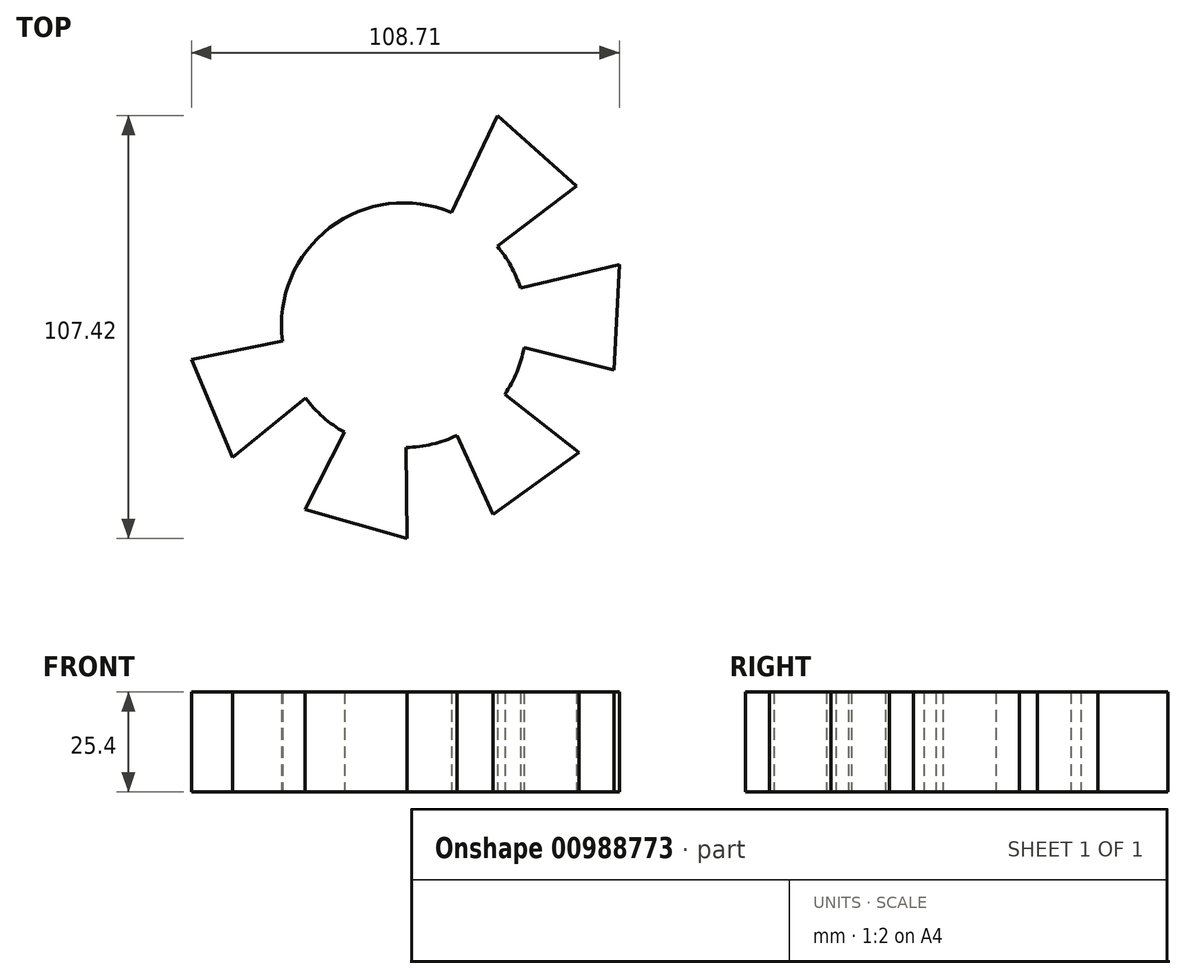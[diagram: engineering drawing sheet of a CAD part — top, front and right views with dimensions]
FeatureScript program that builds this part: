
annotation { "Feature Type Name" : "Feature", "Feature Type Description" : "" }
export const myFeature = defineFeature(function(context is Context, id is Id, definition is map)
    precondition{}
    {
        {
            var Q0;
            Q0=qCreatedBy(makeId("Top.planeOp"),FACE);
            var sketch = newSketch(context, id + "F0", { "sketchPlane" : qUnion([Q0])});
            skCircle(sketch, "E0", {"center": v(0, -2.16) * mm, "radius": 31.08 * mm});
            skLineSegment(sketch, "E1", {"start": v(12.13, 26.46) * mm, "end": v(23.74, 51.09) * mm});
            skLineSegment(sketch, "E2", {"start": v(23.74, 51.09) * mm, "end": v(43.9, 33.24) * mm});
            skLineSegment(sketch, "E3", {"start": v(43.9, 33.24) * mm, "end": v(23.74, 17.9) * mm});
            skLineSegment(sketch, "E4.1.0", {"start": v(-13.12, 25.98) * mm, "end": v(-25.14, 50.42) * mm});
            skLineSegment(sketch, "E4.1.1", {"start": v(-25.14, 50.42) * mm, "end": v(1.38, 55.04) * mm});
            skLineSegment(sketch, "E4.1.2", {"start": v(1.38, 55.04) * mm, "end": v(0.8, 29.73) * mm});
            skLineSegment(sketch, "E4.2.0", {"start": v(-28.5, 5.94) * mm, "end": v(-55.09, 11.78) * mm});
            skLineSegment(sketch, "E4.2.1", {"start": v(-55.09, 11.78) * mm, "end": v(-42.17, 35.4) * mm});
            skLineSegment(sketch, "E4.2.2", {"start": v(-42.17, 35.4) * mm, "end": v(-22.74, 19.17) * mm});
            skLineSegment(sketch, "E4.3.0", {"start": v(-22.4, -18.58) * mm, "end": v(-43.56, -35.72) * mm});
            skLineSegment(sketch, "E4.3.1", {"start": v(-43.56, -35.72) * mm, "end": v(-53.97, -10.9) * mm});
            skLineSegment(sketch, "E4.3.2", {"start": v(-53.97, -10.9) * mm, "end": v(-29.16, -5.83) * mm});
            skLineSegment(sketch, "E4.4.0", {"start": v(0.55, -29.1) * mm, "end": v(0.77, -56.33) * mm});
            skLineSegment(sketch, "E4.4.1", {"start": v(0.77, -56.33) * mm, "end": v(-25.12, -49) * mm});
            skLineSegment(sketch, "E4.4.2", {"start": v(-25.12, -49) * mm, "end": v(-13.63, -26.43) * mm});
            skLineSegment(sketch, "E4.5.0", {"start": v(23.1, -17.71) * mm, "end": v(44.52, -34.52) * mm});
            skLineSegment(sketch, "E4.5.1", {"start": v(44.52, -34.52) * mm, "end": v(22.64, -50.19) * mm});
            skLineSegment(sketch, "E4.5.2", {"start": v(22.64, -50.19) * mm, "end": v(12.17, -27.13) * mm});
            skLineSegment(sketch, "E4.6.0", {"start": v(28.25, 7.01) * mm, "end": v(54.74, 13.29) * mm});
            skLineSegment(sketch, "E4.6.1", {"start": v(54.74, 13.29) * mm, "end": v(53.35, -13.59) * mm});
            skLineSegment(sketch, "E4.6.2", {"start": v(53.35, -13.59) * mm, "end": v(28.8, -7.4) * mm});
            skPoint(sketch, "E4.center", {"position": v(0, 0) * mm});
            skSolve(sketch);
        }
        {
            var Q0;
            Q0 = qSketchRegion(id + "F0", true);
            extrude(context, id + "F1", {"entities" : qUnion([Q0]), "depth" : 25.4 * mm, "offsetDistance" : 25.4 * mm});
        }
    });
